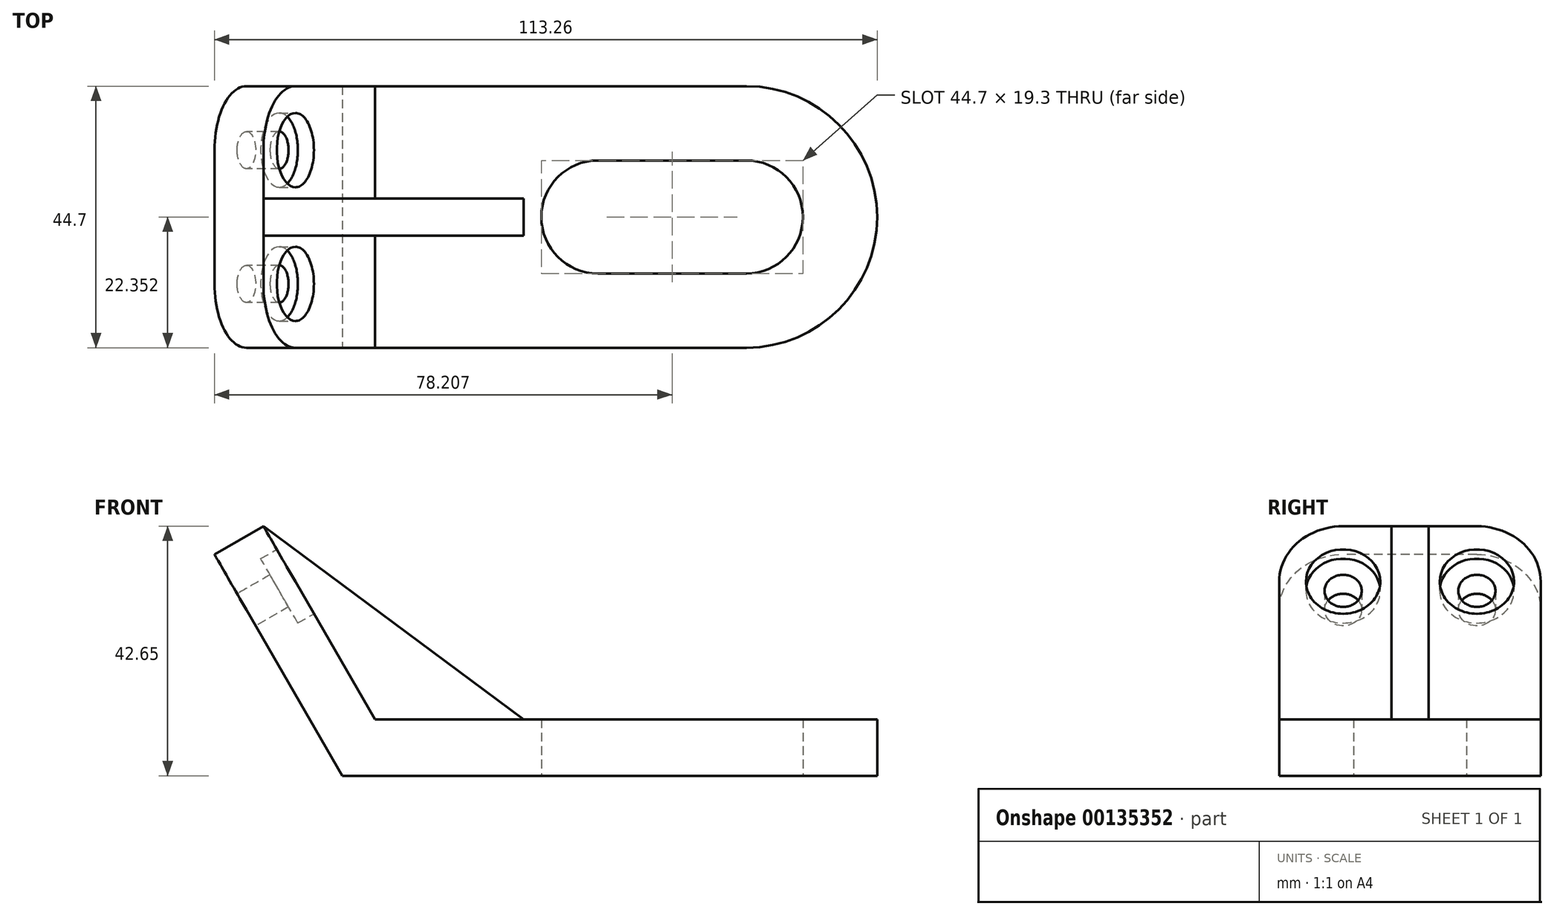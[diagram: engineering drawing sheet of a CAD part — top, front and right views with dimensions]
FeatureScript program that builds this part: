
annotation { "Feature Type Name" : "Feature", "Feature Type Description" : "" }
export const myFeature = defineFeature(function(context is Context, id is Id, definition is map)
    precondition{}
    {
        {
            var Q0;
            Q0=qCreatedBy(makeId("Top.planeOp"),FACE);
            var sketch = newSketch(context, id + "F0", { "sketchPlane" : qUnion([Q0])});
            skLineSegment(sketch, "E0", {"start": v(0, 44.7) * mm, "end": v(83.43, 44.7) * mm});
            skLineSegment(sketch, "E1", {"start": v(19.93, 44.7) * mm, "end": v(0, 44.7) * mm});
            skLineSegment(sketch, "E2", {"start": v(19.93, 44.7) * mm, "end": v(19.93, 0) * mm});
            skLineSegment(sketch, "E3", {"start": v(0, 0) * mm, "end": v(19.93, 0) * mm});
            skLineSegment(sketch, "E4", {"start": v(0, 0) * mm, "end": v(83.43, 0) * mm});
            skLineSegment(sketch, "E5", {"start": v(83.43, 0) * mm, "end": v(83.43, 44.7) * mm});
            skArc(sketch, "E6", {"start": v(83.43, 0) * mm, "mid": v(105.78, 22.35) * mm, "end": v(83.43, 44.7) * mm});
            skArc(sketch, "E7", {"start": v(58.03, 32) * mm, "mid": v(48.38, 22.35) * mm, "end": v(58.03, 12.7) * mm});
            skArc(sketch, "E8", {"start": v(83.43, 12.7) * mm, "mid": v(93.08, 22.35) * mm, "end": v(83.43, 32) * mm});
            skLineSegment(sketch, "E9", {"start": v(73.78, 22.35) * mm, "end": v(83.43, 22.35) * mm});
            skLineSegment(sketch, "E10", {"start": v(83.43, 22.35) * mm, "end": v(83.43, 22.35) * mm});
            skLineSegment(sketch, "E11", {"start": v(58.03, 32) * mm, "end": v(83.43, 32) * mm});
            skLineSegment(sketch, "E12", {"start": v(58.03, 12.7) * mm, "end": v(83.43, 12.7) * mm});
            skLineSegment(sketch, "E13", {"start": v(58.03, 22.35) * mm, "end": v(73.78, 22.35) * mm});
            skSolve(sketch);
        }
        {
            var Q0;
            {var subQ2=sQuery(id+"F0.wireOp",EDGE,"E0");Q0=makeQuery(id+"F0.imprint","IMPRINT",FACE,{"disambiguationData":[TD([[makeQuery(id+"F0.imprint","IMPRINT",EDGE,{"derivedFrom":subQ2}),-1.0]])]});}
            extrude(context, id + "F1", {"entities" : qUnion([Q0]), "depth" : 9.65 * mm});
        }
        {
            var Q0;
            {var subQ0=sQuery(id+"F0.wireOp",EDGE,"E6");Q0=makeQuery(id+"F0.imprint","IMPRINT",FACE,{"disambiguationData":[TD([[makeQuery(id+"F0.imprint","IMPRINT",EDGE,{"derivedFrom":subQ0}),1.0]])]});}
            extrude(context, id + "F2", {"entities" : qUnion([Q0]), "operationType" : NewBodyOperationType.ADD, "depth" : 9.65 * mm});
        }
        {
            var Q0;
            Q0=makeQuery(id+"F1.opExtrude","SWEPT_FACE",FACE,{"disambiguationData":[OSD([sQuery(id+"F0.wireOp",EDGE,"E4")])]});
            var sketch = newSketch(context, id + "F3", { "sketchPlane" : qUnion([Q0])});
            skLineSegment(sketch, "E14", {"start": v(19.93, 9.65) * mm, "end": v(0.88, 42.65) * mm});
            skLineSegment(sketch, "E15", {"start": v(0.88, 42.65) * mm, "end": v(-7.48, 37.82) * mm});
            skLineSegment(sketch, "E16", {"start": v(-7.48, 37.82) * mm, "end": v(14.35, 0) * mm});
            skLineSegment(sketch, "E17", {"start": v(14.35, 0) * mm, "end": v(19.93, 0) * mm});
            skSolve(sketch);
        }
        {
            var Q0;
            Q0=makeQuery(id+"F3.imprint","IMPRINT",FACE,{"disambiguationData":[TD([[makeQuery(id+"F3.imprint","IMPRINT",EDGE,{"derivedFrom":sQuery(id+"F3.wireOp",EDGE,"E14")}),1.0]])]});
            extrude(context, id + "F4", {"entities" : qUnion([Q0]), "operationType" : NewBodyOperationType.ADD, "oppositeDirection" : true, "depth" : 44.7 * mm});
        }
        {
            var Q0;
            Q0=makeQuery(id+"F4.opExtrude","CAP_EDGE",EDGE,{"disambiguationData":[OSD([sQuery(id+"F3.wireOp",EDGE,"E15")])],"isStart":true});
            var Q1;
            Q1=makeQuery(id+"F4.opExtrude","CAP_EDGE",EDGE,{"disambiguationData":[OSD([sQuery(id+"F3.wireOp",EDGE,"E15")])],"isStart":false});
            fillet(context, id + "F5", {"entities" : qUnion([Q0, Q1]), "radius" : 10.92 * mm, "tangentPropagation" : true, "allowEdgeOverflow" : false});
        }
        {
            var Q0;
            Q0=makeQuery(id+"F4.opExtrude","SWEPT_FACE",FACE,{"disambiguationData":[OSD([sQuery(id+"F3.wireOp",EDGE,"E14")])]});
            var sketch = newSketch(context, id + "F6", { "sketchPlane" : qUnion([Q0])});
            skLineSegment(sketch, "E18", {"start": v(0, 25.57) * mm, "end": v(44.7, 25.57) * mm});
            skLineSegment(sketch, "E19", {"start": v(10.92, 36.5) * mm, "end": v(10.92, 25.57) * mm});
            skLineSegment(sketch, "E20", {"start": v(33.78, 36.5) * mm, "end": v(33.78, 25.57) * mm});
            skCircle(sketch, "E21", {"center": v(10.92, 25.57) * mm, "radius": 6.35 * mm});
            skCircle(sketch, "E22", {"center": v(33.78, 25.57) * mm, "radius": 6.35 * mm});
            skSolve(sketch);
        }
        {
            var Q0;
            {var subQ0=sQuery(id+"F6.wireOp",EDGE,"E18");var subQ1=makeQuery(id+"F6.imprint","INTERSECT",VERTEX,{"derivedFrom":[subQ0,sQuery(id+"F6.wireOp",EDGE,"E19")]});Q0=makeQuery(id+"F6.imprint","IMPRINT",FACE,{"disambiguationData":[TD([[makeQuery(id+"F6.imprint","IMPRINT",EDGE,{"disambiguationData":[TD([[subQ1,1.0]])],"derivedFrom":subQ0}),-1.0]])]});}
            var Q1;
            {var subQ0=sQuery(id+"F6.wireOp",EDGE,"E19");var subQ1=sQuery(id+"F6.wireOp",EDGE,"E18");var subQ2=makeQuery(id+"F6.imprint","INTERSECT",VERTEX,{"derivedFrom":[subQ1,subQ0]});Q1=makeQuery(id+"F6.imprint","IMPRINT",FACE,{"disambiguationData":[TD([[makeQuery(id+"F6.imprint","IMPRINT",EDGE,{"disambiguationData":[TD([[subQ2,-1.0]])],"derivedFrom":subQ1}),1.0]])]});}
            var Q2;
            {var subQ0=sQuery(id+"F6.wireOp",EDGE,"E19");var subQ1=sQuery(id+"F6.wireOp",EDGE,"E18");var subQ2=makeQuery(id+"F6.imprint","INTERSECT",VERTEX,{"derivedFrom":[subQ1,subQ0]});Q2=makeQuery(id+"F6.imprint","IMPRINT",FACE,{"disambiguationData":[TD([[makeQuery(id+"F6.imprint","IMPRINT",EDGE,{"disambiguationData":[TD([[subQ2,1.0]])],"derivedFrom":subQ1}),1.0]])]});}
            var Q3;
            {var subQ0=sQuery(id+"F6.wireOp",EDGE,"E20");var subQ1=sQuery(id+"F6.wireOp",EDGE,"E18");var subQ2=makeQuery(id+"F6.imprint","INTERSECT",VERTEX,{"derivedFrom":[subQ1,subQ0]});Q3=makeQuery(id+"F6.imprint","IMPRINT",FACE,{"disambiguationData":[TD([[makeQuery(id+"F6.imprint","IMPRINT",EDGE,{"disambiguationData":[TD([[subQ2,1.0]])],"derivedFrom":subQ1}),1.0]])]});}
            var Q4;
            {var subQ0=sQuery(id+"F6.wireOp",EDGE,"E20");var subQ1=sQuery(id+"F6.wireOp",EDGE,"E18");var subQ2=makeQuery(id+"F6.imprint","INTERSECT",VERTEX,{"derivedFrom":[subQ1,subQ0]});Q4=makeQuery(id+"F6.imprint","IMPRINT",FACE,{"disambiguationData":[TD([[makeQuery(id+"F6.imprint","IMPRINT",EDGE,{"disambiguationData":[TD([[subQ2,-1.0]])],"derivedFrom":subQ1}),1.0]])]});}
            var Q5;
            {var subQ0=sQuery(id+"F6.wireOp",EDGE,"E18");var subQ1=makeQuery(id+"F6.imprint","INTERSECT",VERTEX,{"derivedFrom":[subQ0,sQuery(id+"F6.wireOp",EDGE,"E20")]});Q5=makeQuery(id+"F6.imprint","IMPRINT",FACE,{"disambiguationData":[TD([[makeQuery(id+"F6.imprint","IMPRINT",EDGE,{"disambiguationData":[TD([[subQ1,1.0]])],"derivedFrom":subQ0}),-1.0]])]});}
            extrude(context, id + "F7", {"entities" : qUnion([Q0, Q1, Q2, Q3, Q4, Q5]), "operationType" : NewBodyOperationType.REMOVE, "oppositeDirection" : true, "depth" : 3.17 * mm});
        }
        {
            var Q0;
            Q0=makeQuery(id+"F4.opExtrude","SWEPT_FACE",FACE,{"disambiguationData":[OSD([sQuery(id+"F3.wireOp",EDGE,"E16")])]});
            var sketch = newSketch(context, id + "F8", { "sketchPlane" : qUnion([Q0])});
            skLineSegment(sketch, "E23.0", {"start": v(-33.78, 36.5) * mm, "end": v(-33.78, 25.57) * mm});
            skLineSegment(sketch, "E23.1", {"start": v(0, 25.57) * mm, "end": v(-44.7, 25.57) * mm});
            skLineSegment(sketch, "E23.2", {"start": v(-10.92, 36.5) * mm, "end": v(-10.92, 25.57) * mm});
            skCircle(sketch, "E24", {"center": v(-33.78, 25.57) * mm, "radius": 3.18 * mm});
            skCircle(sketch, "E25", {"center": v(-10.92, 25.57) * mm, "radius": 3.18 * mm});
            skSolve(sketch);
        }
        {
            var Q0;
            {var subQ0=sQuery(id+"F8.wireOp",EDGE,"E23.1");var subQ1=makeQuery(id+"F8.imprint","INTERSECT",VERTEX,{"derivedFrom":[sQuery(id+"F8.wireOp",EDGE,"E23.0"),subQ0]});Q0=makeQuery(id+"F8.imprint","IMPRINT",FACE,{"disambiguationData":[TD([[makeQuery(id+"F8.imprint","IMPRINT",EDGE,{"disambiguationData":[TD([[subQ1,1.0]])],"derivedFrom":subQ0}),1.0]])]});}
            var Q1;
            {var subQ0=sQuery(id+"F8.wireOp",EDGE,"E23.1");var subQ1=sQuery(id+"F8.wireOp",EDGE,"E23.0");var subQ2=makeQuery(id+"F8.imprint","INTERSECT",VERTEX,{"derivedFrom":[subQ1,subQ0]});Q1=makeQuery(id+"F8.imprint","IMPRINT",FACE,{"disambiguationData":[TD([[makeQuery(id+"F8.imprint","IMPRINT",EDGE,{"disambiguationData":[TD([[subQ2,1.0]])],"derivedFrom":subQ1}),-1.0]])]});}
            var Q2;
            {var subQ0=sQuery(id+"F8.wireOp",EDGE,"E23.1");var subQ1=sQuery(id+"F8.wireOp",EDGE,"E23.0");var subQ2=makeQuery(id+"F8.imprint","INTERSECT",VERTEX,{"derivedFrom":[subQ1,subQ0]});Q2=makeQuery(id+"F8.imprint","IMPRINT",FACE,{"disambiguationData":[TD([[makeQuery(id+"F8.imprint","IMPRINT",EDGE,{"disambiguationData":[TD([[subQ2,1.0]])],"derivedFrom":subQ1}),1.0]])]});}
            var Q3;
            {var subQ0=sQuery(id+"F8.wireOp",EDGE,"E23.2");var subQ1=sQuery(id+"F8.wireOp",EDGE,"E23.1");var subQ2=makeQuery(id+"F8.imprint","INTERSECT",VERTEX,{"derivedFrom":[subQ1,subQ0]});Q3=makeQuery(id+"F8.imprint","IMPRINT",FACE,{"disambiguationData":[TD([[makeQuery(id+"F8.imprint","IMPRINT",EDGE,{"disambiguationData":[TD([[subQ2,-1.0]])],"derivedFrom":subQ1}),-1.0]])]});}
            var Q4;
            {var subQ0=sQuery(id+"F8.wireOp",EDGE,"E23.2");var subQ1=sQuery(id+"F8.wireOp",EDGE,"E23.1");var subQ2=makeQuery(id+"F8.imprint","INTERSECT",VERTEX,{"derivedFrom":[subQ1,subQ0]});Q4=makeQuery(id+"F8.imprint","IMPRINT",FACE,{"disambiguationData":[TD([[makeQuery(id+"F8.imprint","IMPRINT",EDGE,{"disambiguationData":[TD([[subQ2,1.0]])],"derivedFrom":subQ1}),-1.0]])]});}
            var Q5;
            {var subQ0=sQuery(id+"F8.wireOp",EDGE,"E23.1");var subQ1=makeQuery(id+"F8.imprint","INTERSECT",VERTEX,{"derivedFrom":[subQ0,sQuery(id+"F8.wireOp",EDGE,"E23.2")]});Q5=makeQuery(id+"F8.imprint","IMPRINT",FACE,{"disambiguationData":[TD([[makeQuery(id+"F8.imprint","IMPRINT",EDGE,{"disambiguationData":[TD([[subQ1,1.0]])],"derivedFrom":subQ0}),1.0]])]});}
            extrude(context, id + "F9", {"entities" : qUnion([Q0, Q1, Q2, Q3, Q4, Q5]), "operationType" : NewBodyOperationType.REMOVE, "endBound" : BoundingType.THROUGH_ALL, "oppositeDirection" : true, "depth" : 25.4 * mm});
        }
        {
            var Q0;
            {var subQ0=sQuery(id+"F0.wireOp",EDGE,"E4");Q0=makeQuery(id+"F4.boolean.opBoolean","MERGE",FACE,{"derivedFrom":[makeQuery(id+"F1.opExtrude","SWEPT_FACE",FACE,{"disambiguationData":[OSD([subQ0])]}),makeQuery(id+"F4.opExtrude","CAP_FACE",FACE,{"disambiguationData":[OSD([sQuery(id+"F0.wireOp",EDGE,"E2"),subQ0,sQuery(id+"F3.wireOp",EDGE,"E14"),sQuery(id+"F3.wireOp",EDGE,"E15"),sQuery(id+"F3.wireOp",EDGE,"E16"),sQuery(id+"F3.wireOp",EDGE,"E17")])],"isStart":true})]});}
            cPlane(context, id + "F10", {"entities" : qUnion([Q0]), "cplaneType" : CPlaneType.OFFSET, "offset" : 22.35 * mm, "oppositeDirection" : true, "width" : 152.4 * mm, "height" : 152.4 * mm});
        }
        {
            var Q0;
            Q0=qCreatedBy(id+"F10.planeOp",FACE);
            var sketch = newSketch(context, id + "F11", { "sketchPlane" : qUnion([Q0])});
            skLineSegment(sketch, "E26.0", {"start": v(0.88, 42.65) * mm, "end": v(-7.48, 37.82) * mm});
            skLineSegment(sketch, "E27.0", {"start": v(19.93, 9.65) * mm, "end": v(0.88, 42.65) * mm});
            skLineSegment(sketch, "E28.0", {"start": v(-7.48, 37.82) * mm, "end": v(14.35, 0) * mm});
            skLineSegment(sketch, "E29.0", {"start": v(19.93, 9.65) * mm, "end": v(83.43, 9.65) * mm});
            skLineSegment(sketch, "E30.0", {"start": v(14.35, 0) * mm, "end": v(83.43, 0) * mm});
            skLineSegment(sketch, "E31", {"start": v(0.88, 42.65) * mm, "end": v(45.33, 9.65) * mm});
            skSolve(sketch);
        }
        {
            var Q0;
            {var subQ0=sQuery(id+"F11.wireOp",EDGE,"E27.0");Q0=makeQuery(id+"F11.imprint","IMPRINT",FACE,{"disambiguationData":[TD([[makeQuery(id+"F11.imprint","IMPRINT",EDGE,{"derivedFrom":subQ0}),-1.0]])]});}
            extrude(context, id + "F12", {"entities" : qUnion([Q0]), "operationType" : NewBodyOperationType.ADD, "endBound" : BoundingType.SYMMETRIC, "depth" : 6.35 * mm});
        }
    });
